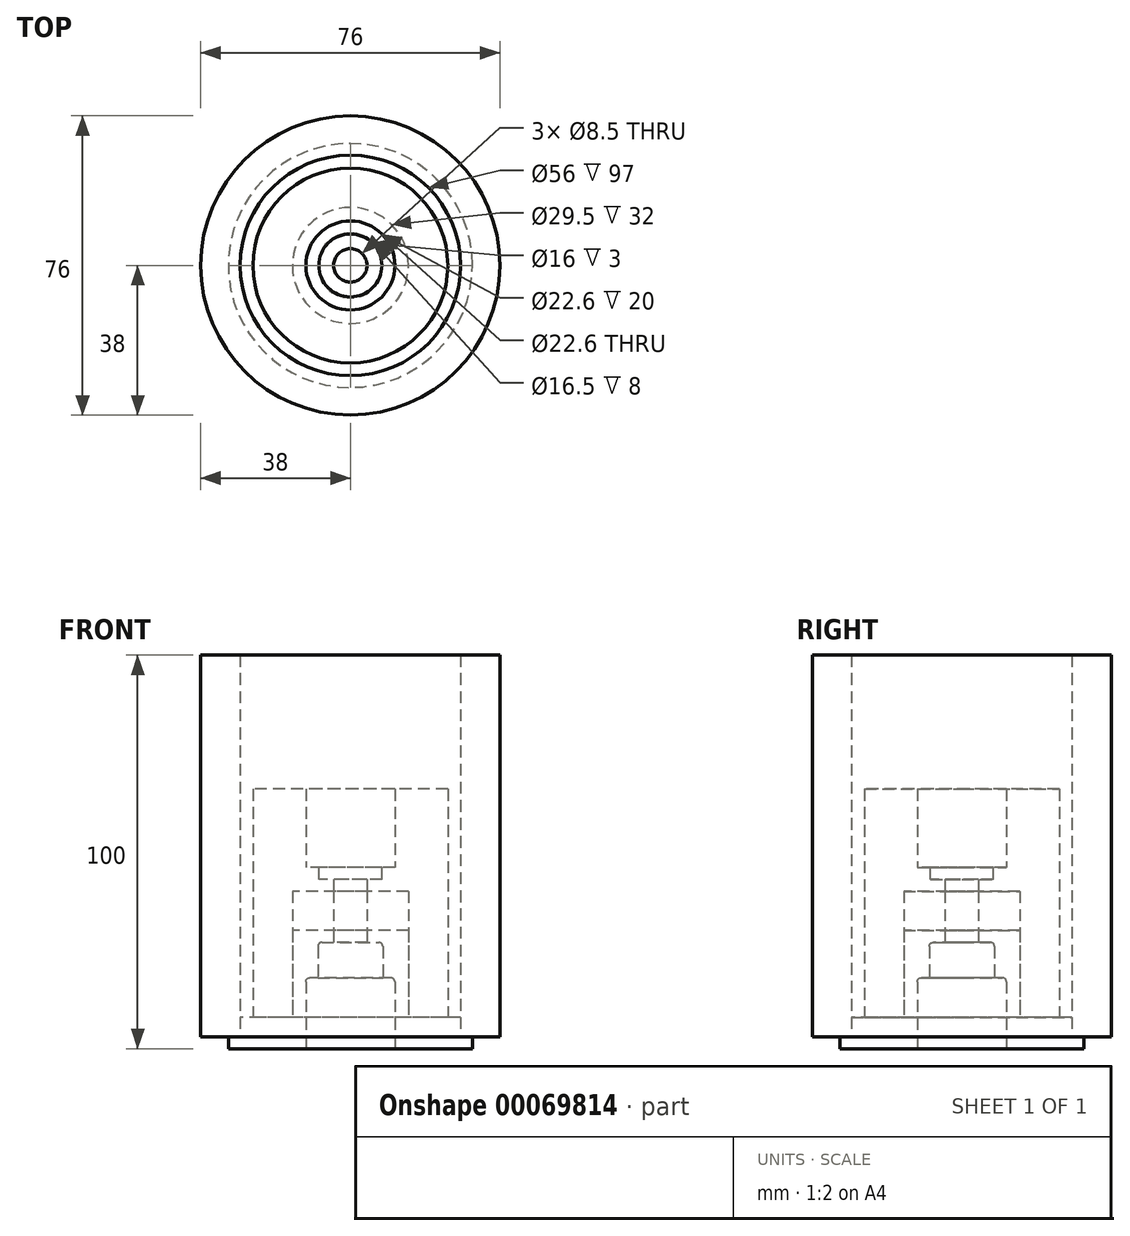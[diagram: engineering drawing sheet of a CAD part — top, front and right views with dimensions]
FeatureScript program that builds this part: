
annotation { "Feature Type Name" : "Feature", "Feature Type Description" : "" }
export const myFeature = defineFeature(function(context is Context, id is Id, definition is map)
    precondition{}
    {
        {
            var Q0;
            Q0=qCreatedBy(makeId("Top.planeOp"),FACE);
            var sketch = newSketch(context, id + "F0", { "sketchPlane" : qUnion([Q0])});
            skCircle(sketch, "E0", {"center": v(0, 0) * mm, "radius": 14.75 * mm});
            skCircle(sketch, "E1", {"center": v(0, 0) * mm, "radius": 28 * mm});
            skCircle(sketch, "E2.0", {"center": v(0, 0) * mm, "radius": 31 * mm});
            skCircle(sketch, "E3", {"center": v(0, 0) * mm, "radius": 11.3 * mm});
            skCircle(sketch, "E4", {"center": v(0, 0) * mm, "radius": 4.25 * mm});
            skSolve(sketch);
        }
        {
            var Q0;
            Q0=makeQuery(id+"F0.imprint","IMPRINT",FACE,{"disambiguationData":[TD([[makeQuery(id+"F0.imprint","IMPRINT",EDGE,{"derivedFrom":sQuery(id+"F0.wireOp",EDGE,"E1")}),-1.0]])]});
            extrude(context, id + "F1", {"entities" : qUnion([Q0]), "depth" : 3 * mm});
        }
        {
            var Q0;
            Q0=makeQuery(id+"F0.imprint","IMPRINT",FACE,{"disambiguationData":[TD([[makeQuery(id+"F0.imprint","IMPRINT",EDGE,{"derivedFrom":sQuery(id+"F0.wireOp",EDGE,"E0")}),-1.0]])]});
            extrude(context, id + "F2", {"entities" : qUnion([Q0]), "operationType" : NewBodyOperationType.ADD, "depth" : 8 * mm});
        }
        {
            var Q0;
            Q0=makeQuery(id+"F0.imprint","IMPRINT",FACE,{"disambiguationData":[TD([[makeQuery(id+"F0.imprint","IMPRINT",EDGE,{"derivedFrom":sQuery(id+"F0.wireOp",EDGE,"E0")}),1.0]])]});
            var Q1;
            Q1=makeQuery(id+"F0.imprint","IMPRINT",FACE,{"disambiguationData":[TD([[makeQuery(id+"F0.imprint","IMPRINT",EDGE,{"derivedFrom":sQuery(id+"F0.wireOp",EDGE,"E3")}),1.0]])]});
            extrude(context, id + "F3", {"entities" : qUnion([Q0, Q1]), "operationType" : NewBodyOperationType.ADD, "depth" : 30 * mm});
        }
        {
            var Q0;
            Q0=makeQuery(id+"F0.imprint","IMPRINT",FACE,{"disambiguationData":[TD([[makeQuery(id+"F0.imprint","IMPRINT",EDGE,{"derivedFrom":sQuery(id+"F0.wireOp",EDGE,"E3")}),1.0]])]});
            extrude(context, id + "F4", {"entities" : qUnion([Q0]), "operationType" : NewBodyOperationType.REMOVE, "depth" : 18 * mm});
        }
        {
            var Q0;
            Q0=makeQuery(id+"F4.boolean.opBoolean","COPY",FACE,{"derivedFrom":makeQuery(id+"F4.opExtrude","CAP_FACE",FACE,{"disambiguationData":[OSD([sQuery(id+"F0.wireOp",EDGE,"E3"),sQuery(id+"F0.wireOp",EDGE,"E4")])],"isStart":false})});
            var sketch = newSketch(context, id + "F5", { "sketchPlane" : qUnion([Q0])});
            skCircle(sketch, "E5", {"center": v(0, 0) * mm, "radius": 8.25 * mm});
            skSolve(sketch);
        }
        {
            var Q0;
            Q0=makeQuery(id+"F5.imprint","IMPRINT",FACE,{"disambiguationData":[TD([[makeQuery(id+"F5.imprint","IMPRINT",EDGE,{"derivedFrom":sQuery(id+"F5.wireOp",EDGE,"E5")}),1.0]])]});
            extrude(context, id + "F6", {"entities" : qUnion([Q0]), "operationType" : NewBodyOperationType.REMOVE, "oppositeDirection" : true, "depth" : 9 * mm});
        }
        {
            var Q0;
            Q0=makeQuery(id+"F4.boolean.opBoolean","COPY",EDGE,{"derivedFrom":makeQuery(id+"F4.opExtrude","CAP_EDGE",EDGE,{"disambiguationData":[OSD([sQuery(id+"F0.wireOp",EDGE,"E3")])],"isStart":false})});
            var Q1;
            Q1=makeQuery(id+"F6.boolean.opBoolean","COPY",EDGE,{"derivedFrom":makeQuery(id+"F6.opExtrude","CAP_EDGE",EDGE,{"disambiguationData":[OSD([sQuery(id+"F5.wireOp",EDGE,"E5")])],"isStart":false})});
            fillet(context, id + "F7", {"entities" : qUnion([Q0, Q1]), "radius" : 1 * mm, "tangentPropagation" : true, "allowEdgeOverflow" : false});
        }
        {
            var Q0;
            Q0=makeQuery(id+"F1.opExtrude","CAP_FACE",FACE,{"disambiguationData":[OSD([sQuery(id+"F0.wireOp",EDGE,"E1"),sQuery(id+"F0.wireOp",EDGE,"E2.0")])],"isStart":false});
            var sketch = newSketch(context, id + "F8", { "sketchPlane" : qUnion([Q0])});
            skCircle(sketch, "E6.0", {"center": v(0, 0) * mm, "radius": 28 * mm});
            skCircle(sketch, "E7.0", {"center": v(0, 0) * mm, "radius": 38 * mm});
            skSolve(sketch);
        }
        {
            var Q0;
            Q0=makeQuery(id+"F8.imprint","IMPRINT",FACE,{"disambiguationData":[TD([[makeQuery(id+"F8.imprint","IMPRINT",EDGE,{"derivedFrom":sQuery(id+"F8.wireOp",EDGE,"E6.0")}),-1.0]])]});
            var Q1;
            Q1=makeQuery(id+"F8.imprint","IMPRINT",FACE,{"disambiguationData":[TD([[makeQuery(id+"F8.imprint","IMPRINT",EDGE,{"derivedFrom":sQuery(id+"F8.wireOp",EDGE,"E7.0")}),1.0]])]});
            extrude(context, id + "F9", {"entities" : qUnion([Q0, Q1]), "depth" : 97 * mm});
        }
        {
            var Q0;
            Q0=makeQuery(id+"F2.opExtrude","CAP_FACE",FACE,{"disambiguationData":[OSD([sQuery(id+"F0.wireOp",EDGE,"E0"),sQuery(id+"F0.wireOp",EDGE,"E1")])],"isStart":false});
            var sketch = newSketch(context, id + "F10", { "sketchPlane" : qUnion([Q0])});
            skCircle(sketch, "E8.0", {"center": v(0, 0) * mm, "radius": 14.75 * mm});
            skCircle(sketch, "E9.0", {"center": v(0, 0) * mm, "radius": 24.75 * mm});
            skSolve(sketch);
        }
        {
            var Q0;
            Q0=makeQuery(id+"F10.imprint","IMPRINT",FACE,{"disambiguationData":[TD([[makeQuery(id+"F10.imprint","IMPRINT",EDGE,{"derivedFrom":sQuery(id+"F10.wireOp",EDGE,"E8.0")}),-1.0]])]});
            extrude(context, id + "F11", {"entities" : qUnion([Q0]), "depth" : 58 * mm});
        }
        {
            var Q0;
            Q0=makeQuery(id+"F3.opExtrude","CAP_FACE",FACE,{"disambiguationData":[OSD([sQuery(id+"F0.wireOp",EDGE,"E0"),sQuery(id+"F0.wireOp",EDGE,"E4")])],"isStart":false});
            extrude(context, id + "F12", {"entities" : qUnion([Q0]), "depth" : 10 * mm});
        }
        {
            var Q0;
            Q0=makeQuery(id+"F12.opExtrude","CAP_FACE",FACE,{"disambiguationData":[OSD([sQuery(id+"F0.wireOp",EDGE,"E0"),sQuery(id+"F0.wireOp",EDGE,"E4")])],"isStart":false});
            var sketch = newSketch(context, id + "F13", { "sketchPlane" : qUnion([Q0])});
            skCircle(sketch, "E10", {"center": v(0, 0) * mm, "radius": 11.3 * mm});
            skSolve(sketch);
        }
        {
            var Q0;
            Q0=makeQuery(id+"F13.imprint","IMPRINT",FACE,{"disambiguationData":[TD([[makeQuery(id+"F13.imprint","IMPRINT",EDGE,{"derivedFrom":sQuery(id+"F13.wireOp",EDGE,"E10")}),-1.0]])]});
            var Q1;
            Q1=makeQuery(id+"F13.imprint","IMPRINT",FACE,{"disambiguationData":[TD([[makeQuery(id+"F13.imprint","IMPRINT",EDGE,{"derivedFrom":sQuery(id+"F13.wireOp",EDGE,"E10")}),1.0]])]});
            extrude(context, id + "F14", {"entities" : qUnion([Q0, Q1]), "depth" : 6 * mm});
        }
        {
            var Q0;
            Q0=makeQuery(id+"F14.opExtrude","CAP_FACE",FACE,{"disambiguationData":[OSD([sQuery(id+"F0.wireOp",EDGE,"E0"),sQuery(id+"F0.wireOp",EDGE,"E4")])],"isStart":false});
            var sketch = newSketch(context, id + "F15", { "sketchPlane" : qUnion([Q0])});
            skCircle(sketch, "E11.0", {"center": v(0, 0) * mm, "radius": 11.3 * mm});
            skCircle(sketch, "E12", {"center": v(0, 0) * mm, "radius": 8 * mm});
            skSolve(sketch);
        }
        {
            var Q0;
            Q0=makeQuery(id+"F15.imprint","IMPRINT",FACE,{"disambiguationData":[TD([[makeQuery(id+"F15.imprint","IMPRINT",EDGE,{"derivedFrom":sQuery(id+"F15.wireOp",EDGE,"E12")}),1.0]])]});
            extrude(context, id + "F16", {"entities" : qUnion([Q0]), "operationType" : NewBodyOperationType.REMOVE, "oppositeDirection" : true, "depth" : 3 * mm});
        }
        {
            var Q0;
            Q0=makeQuery(id+"F15.imprint","IMPRINT",FACE,{"disambiguationData":[TD([[makeQuery(id+"F15.imprint","IMPRINT",EDGE,{"derivedFrom":sQuery(id+"F15.wireOp",EDGE,"E11.0")}),-1.0]])]});
            var Q1;
            Q1=makeQuery(id+"F11.opExtrude","CAP_FACE",FACE,{"disambiguationData":[OSD([sQuery(id+"F10.wireOp",EDGE,"E8.0"),sQuery(id+"F10.wireOp",EDGE,"E9.0")])],"isStart":false});
            extrude(context, id + "F17", {"entities" : qUnion([Q0]), "operationType" : NewBodyOperationType.ADD, "endBound" : BoundingType.UP_TO_SURFACE, "endBoundEntityFace" : qUnion([Q1]), "depth" : 25 * mm});
        }
    });
